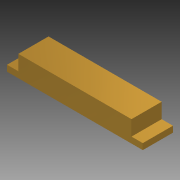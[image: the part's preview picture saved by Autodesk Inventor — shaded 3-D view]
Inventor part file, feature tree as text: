
AUTODESK INVENTOR PART (.ipt)
format: ipt  version: 2013 (Build 170138000, 138)  size: 80,896 bytes
history: native  units: mm
features: extrude x2, sketch x2
ambient origin geometry x8: Origin, YZ Plane, XZ Plane, XY Plane, X Axis, Y Axis, Z Axis, Center Point
bodies: Volumenkörper1 (feature_tree)
feature tree (4):
  extrude  "Extrusion1"  Depth=20.0mm
  extrude  "Extrusion2"  Depth=75.0mm
  sketch  "Skizze1"  dims[d0=90.0mm d1=20.0mm]
  sketch  "Skizze2"  dims[d2=4.0mm d3=0.0mm d4=75.0mm d6=10.0mm d7=0.0mm]
